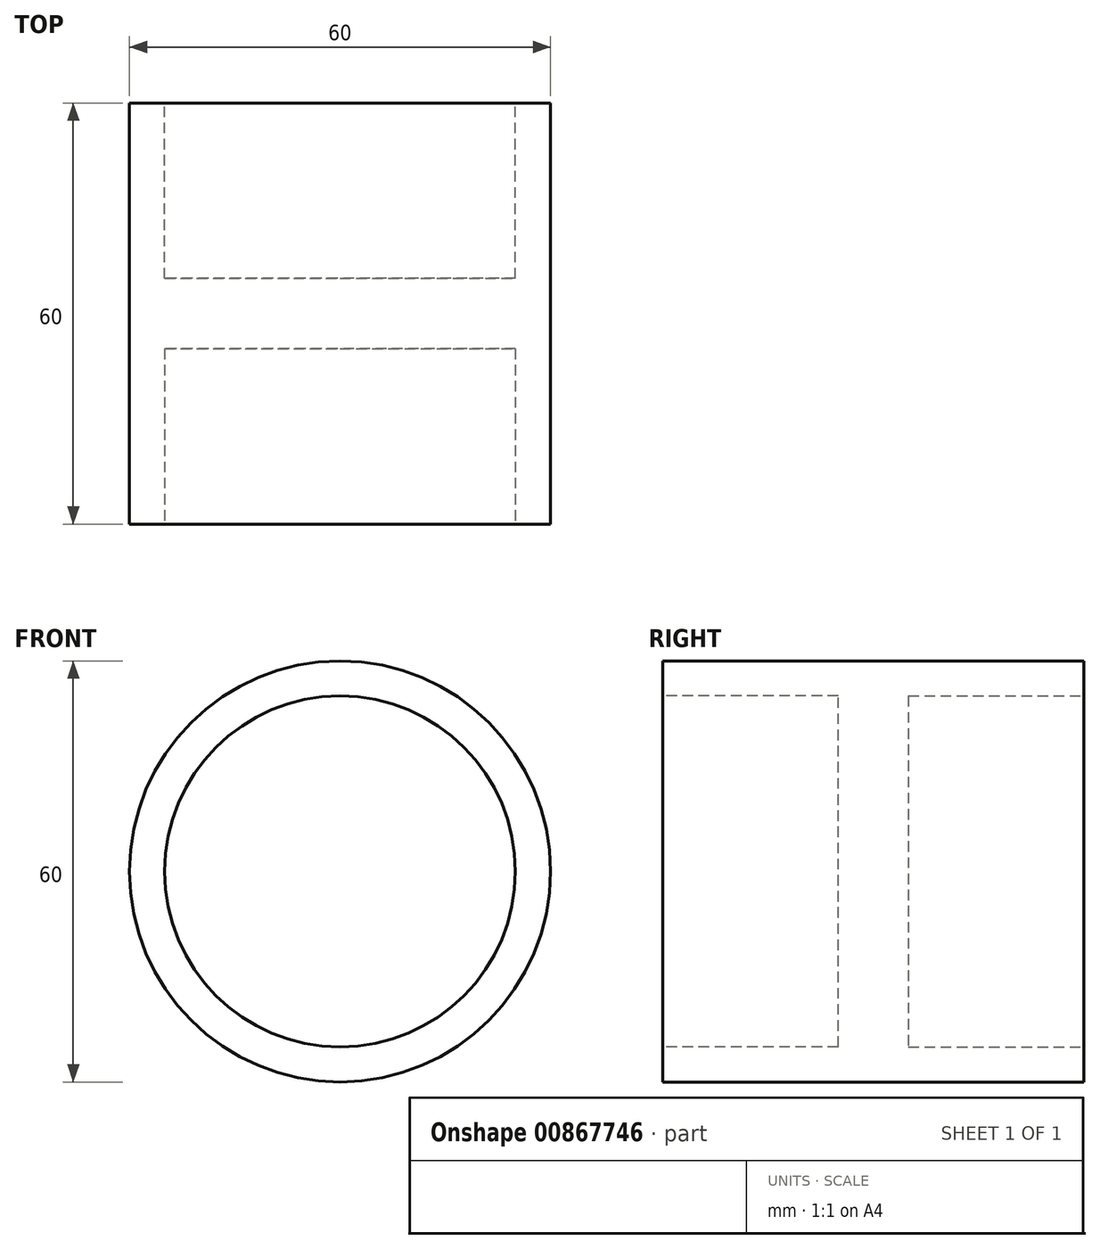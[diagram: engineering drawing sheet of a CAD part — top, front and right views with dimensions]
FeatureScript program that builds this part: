
annotation { "Feature Type Name" : "Feature", "Feature Type Description" : "" }
export const myFeature = defineFeature(function(context is Context, id is Id, definition is map)
    precondition{}
    {
        {
            var Q0;
            Q0=qCreatedBy(makeId("Front.planeOp"),FACE);
            var sketch = newSketch(context, id + "F0", { "sketchPlane" : qUnion([Q0])});
            skCircle(sketch, "E0", {"center": v(0, 0) * mm, "radius": 30 * mm});
            skSolve(sketch);
        }
        {
            var Q0;
            Q0=makeQuery(id+"F0.imprint","IMPRINT",FACE,{"disambiguationData":[TD([[makeQuery(id+"F0.imprint","IMPRINT",EDGE,{"derivedFrom":sQuery(id+"F0.wireOp",EDGE,"E0")}),1.0]])]});
            extrude(context, id + "F1", {"entities" : qUnion([Q0]), "depth" : 30 * mm, "offsetDistance" : 25 * mm});
        }
        {
            var Q0;
            Q0=makeQuery(id+"F1.opExtrude","CAP_FACE",FACE,{"disambiguationData":[OSD([sQuery(id+"F0.wireOp",EDGE,"E0")])],"isStart":true});
            var sketch = newSketch(context, id + "F2", { "sketchPlane" : qUnion([Q0])});
            skCircle(sketch, "E1", {"center": v(0, 0) * mm, "radius": 25 * mm});
            skSolve(sketch);
        }
        {
            var Q0;
            Q0=makeQuery(id+"F2.imprint","IMPRINT",FACE,{"disambiguationData":[TD([[makeQuery(id+"F2.imprint","IMPRINT",EDGE,{"derivedFrom":sQuery(id+"F2.wireOp",EDGE,"E1")}),1.0]])]});
            extrude(context, id + "F3", {"entities" : qUnion([Q0]), "operationType" : NewBodyOperationType.REMOVE, "oppositeDirection" : true, "depth" : 25 * mm, "offsetDistance" : 25 * mm});
        }
        {
            var Q0;
            Q0=makeQuery(id+"F1.opExtrude","CAP_FACE",FACE,{"disambiguationData":[OSD([sQuery(id+"F0.wireOp",EDGE,"E0")])],"isStart":false});
            extrude(context, id + "F4", {"entities" : qUnion([Q0]), "operationType" : NewBodyOperationType.ADD, "depth" : 30 * mm, "offsetDistance" : 25 * mm});
        }
        {
            var Q0;
            Q0=makeQuery(id+"F4.opExtrude","CAP_FACE",FACE,{"disambiguationData":[OSD([sQuery(id+"F0.wireOp",EDGE,"E0")])],"isStart":false});
            var sketch = newSketch(context, id + "F5", { "sketchPlane" : qUnion([Q0])});
            skCircle(sketch, "E2", {"center": v(0, 0) * mm, "radius": 25 * mm});
            skSolve(sketch);
        }
        {
            var Q0;
            Q0=makeQuery(id+"F5.imprint","IMPRINT",FACE,{"disambiguationData":[TD([[makeQuery(id+"F5.imprint","IMPRINT",EDGE,{"derivedFrom":sQuery(id+"F5.wireOp",EDGE,"E2")}),1.0]])]});
            extrude(context, id + "F6", {"entities" : qUnion([Q0]), "operationType" : NewBodyOperationType.REMOVE, "oppositeDirection" : true, "depth" : 25 * mm, "offsetDistance" : 25 * mm});
        }
    });
